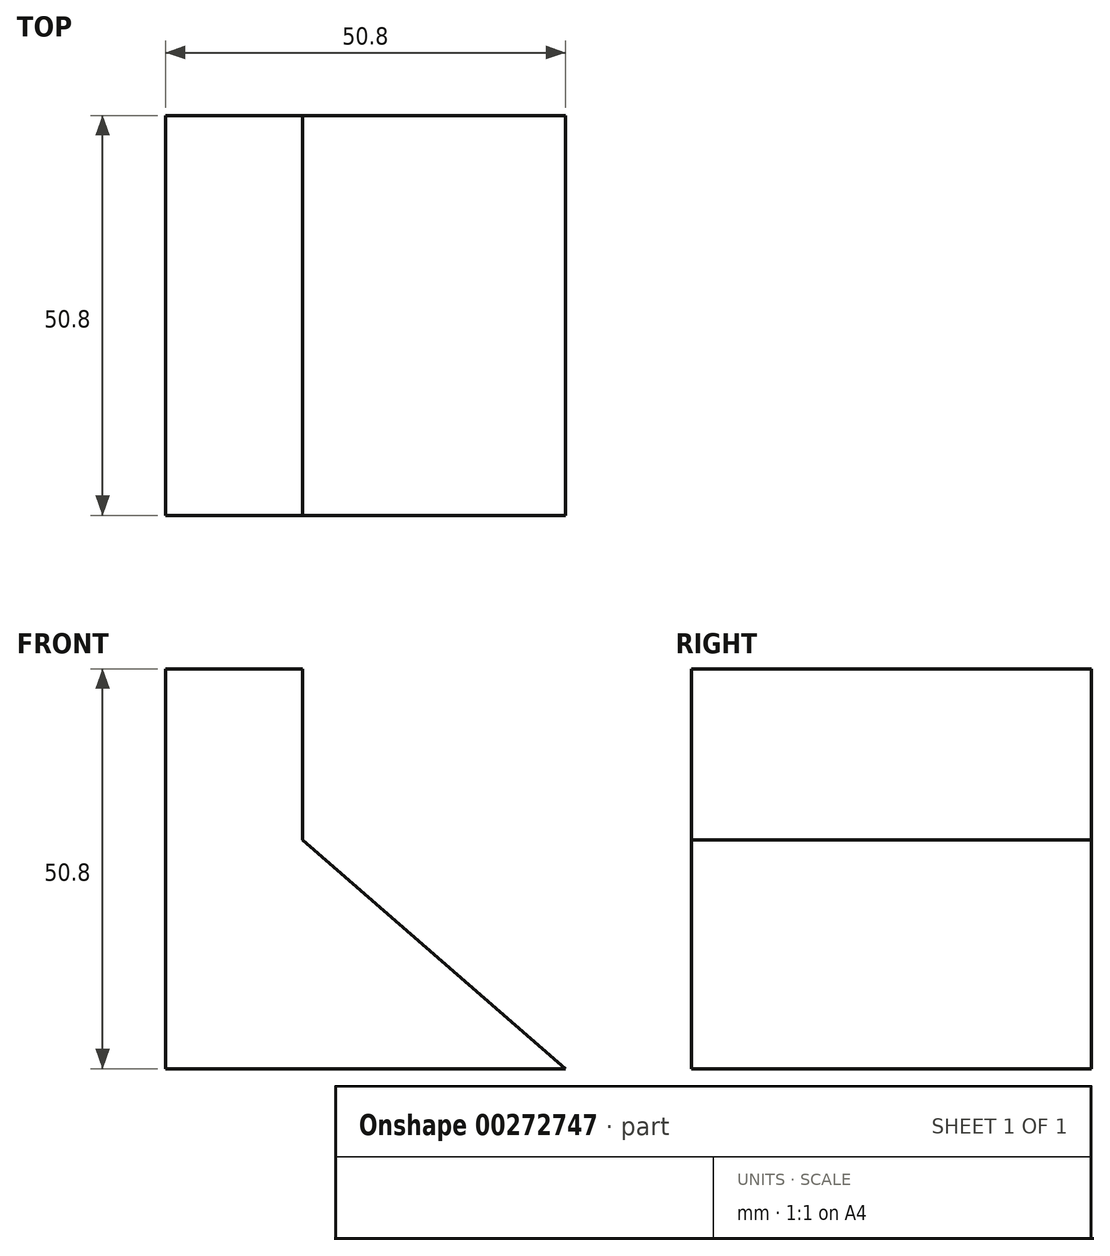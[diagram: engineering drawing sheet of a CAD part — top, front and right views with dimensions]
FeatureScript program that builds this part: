
annotation { "Feature Type Name" : "Feature", "Feature Type Description" : "" }
export const myFeature = defineFeature(function(context is Context, id is Id, definition is map)
    precondition{}
    {
        {
            var Q0;
            Q0=qCreatedBy(makeId("Front.planeOp"),FACE);
            var sketch = newSketch(context, id + "F0", { "sketchPlane" : qUnion([Q0])});
            skLineSegment(sketch, "E0", {"start": v(0, 0) * mm, "end": v(-50.8, 0) * mm});
            skLineSegment(sketch, "E1", {"start": v(-50.8, 0) * mm, "end": v(-50.8, 50.8) * mm});
            skLineSegment(sketch, "E2", {"start": v(-50.8, 50.8) * mm, "end": v(-33.42, 50.8) * mm});
            skLineSegment(sketch, "E3", {"start": v(-33.42, 50.8) * mm, "end": v(-33.42, 29.03) * mm});
            skLineSegment(sketch, "E4", {"start": v(-33.42, 29.03) * mm, "end": v(0, 0) * mm});
            skSolve(sketch);
        }
        {
            var Q0;
            Q0=makeQuery(id+"F0.imprint","IMPRINT",FACE,{"disambiguationData":[TD([[makeQuery(id+"F0.imprint","IMPRINT",EDGE,{"derivedFrom":sQuery(id+"F0.wireOp",EDGE,"E0")}),-1.0]])]});
            extrude(context, id + "F1", {"entities" : qUnion([Q0]), "depth" : 50.8 * mm});
        }
    });
